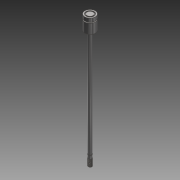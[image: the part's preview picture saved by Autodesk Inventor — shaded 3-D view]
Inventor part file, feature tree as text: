
AUTODESK INVENTOR PART (.ipt)
format: ipt  version: 2014 SP1 (Build 180222100, 222)  size: 189,440 bytes
history: native  units: in
note: dims shown in document units (in); Inventor stores cm internally (conversion verified against a paired STEP export)
features: sketch x4, revolve x1, other x1, helix x1, extrude x1
ambient origin geometry x8: Origin, YZ Plane, XZ Plane, XY Plane, X Axis, Y Axis, Z Axis, Center Point
bodies: Solid1 (feature_tree)
feature tree (8):
  sketch  "Sketch1"  dims[d0=0.1in d2=90.0deg d3=8.2762in]
  revolve  "Revolution1"  Angle=90.0deg
  other  "Work Axis1"
  sketch  "Sketch4"  dims[d4=1.0in d5=0.375in]
  helix  "Coil2"  [1 undecoded]
  extrude  "Extrusion3"  Depth=0.375in
  sketch  "Sketch5"  dims[d22=0.025in]
  sketch  "Sketch6"  dims[d23=0.5in d27=0.025in d28=0.225in d32=0.0625in d33=0.0312in d35=0.5in d36=0.0625in d37=0.01in d38=60.0deg d39=0.025in d40=0.05in d41=0.55in d42=0.3937in d43=0.0in d44=90.0deg d45=90.0deg d46=0.0in d47=0.0in d48=0.5in d49=0.0in d50=0.0in d51=0.25in d52=0.0625in d53=0.0in d54=0.0in]
note: 1 required parameter value undecoded (feature->parameter linkage not recoverable at this tier; creation-order binding heuristic only, values carry confidence <= 0.55)
